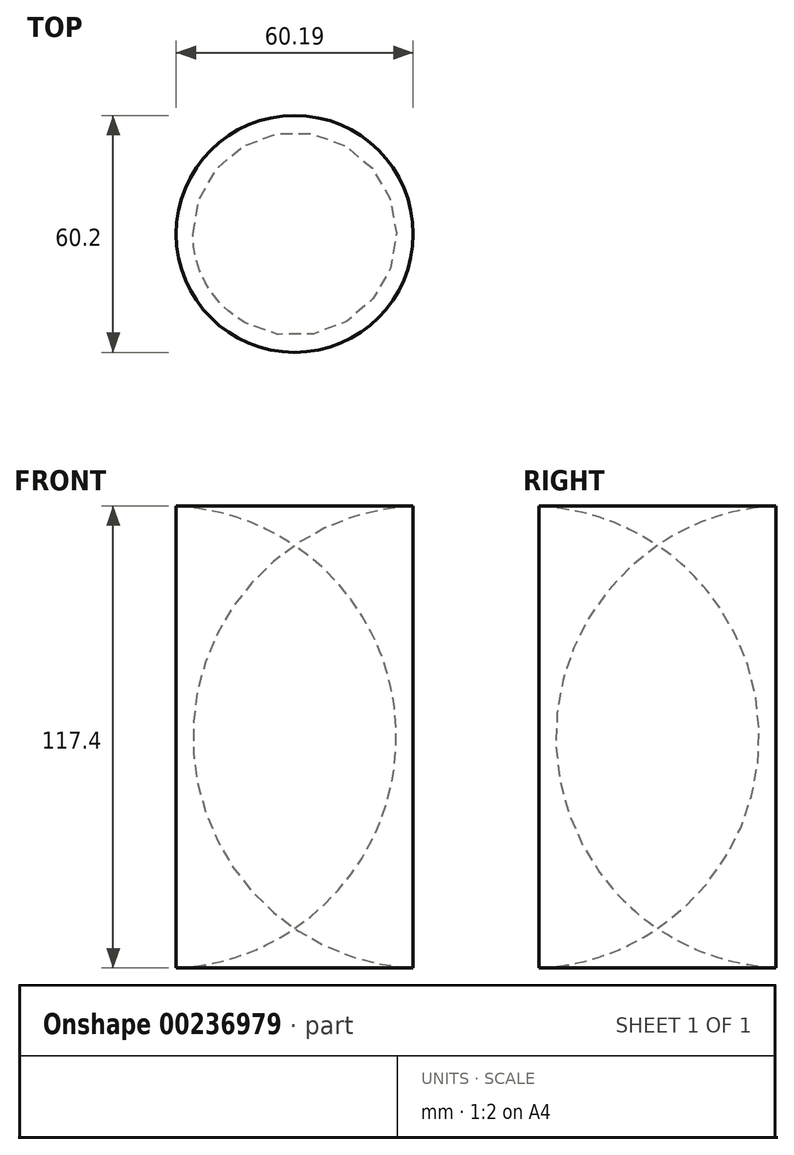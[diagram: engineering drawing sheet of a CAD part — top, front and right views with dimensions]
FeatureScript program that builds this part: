
annotation { "Feature Type Name" : "Feature", "Feature Type Description" : "" }
export const myFeature = defineFeature(function(context is Context, id is Id, definition is map)
    precondition{}
    {
        {
            var Q0;
            Q0=qCreatedBy(makeId("Front.planeOp"),FACE);
            var sketch = newSketch(context, id + "F0", { "sketchPlane" : qUnion([Q0])});
            skLineSegment(sketch, "E0", {"start": v(-40.38, 59.15) * mm, "end": v(-40.38, -55.28) * mm});
            skLineSegment(sketch, "E1", {"start": v(-10.28, 58.85) * mm, "end": v(-10.28, -58.55) * mm});
            skArc(sketch, "E2", {"start": v(-10.28, -58.55) * mm, "mid": v(51.32, 0.15) * mm, "end": v(-10.28, 58.85) * mm});
            skSolve(sketch);
        }
        {
            var Q0;
            Q0 = qSketchRegion(id + "F0", true);
            var Q1;
            Q1=sQuery(id+"F0.wireOp",EDGE,"E0");
            revolve(context, id + "F1", {"entities" : qUnion([Q0]), "axis" : qUnion([Q1]), "revolveType" : RevolveType.FULL});
        }
    });
